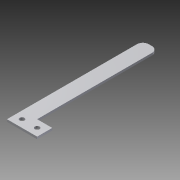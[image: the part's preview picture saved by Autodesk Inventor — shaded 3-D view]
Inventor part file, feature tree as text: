
AUTODESK INVENTOR PART (.ipt)
format: ipt  version: 2015 (Build 190159000, 159)  size: 123,392 bytes
history: native  units: mm
features: sketch x3, extrude x2, other x1, fillet x1, hole x1
ambient origin geometry x8: Origin, YZ Plane, XZ Plane, XY Plane, X Axis, Y Axis, Z Axis, Center Point
bodies: Body1 (feature_tree)
feature tree (8):
  other  "ソリッド1"
  extrude  "押し出し1"  Depth=10.0mm
  fillet  "フィレット1"  Radius=80.0mm
  extrude  "押し出し8"  Depth=1.5mm TaperAngle=0.0deg
  hole  "穴2"  [1 undecoded]
  sketch  "スケッチ1"
  sketch  "スケッチ9"
  sketch  "スケッチ10"
note: 1 required parameter value undecoded (feature->parameter linkage not recoverable at this tier; creation-order binding heuristic only, values carry confidence <= 0.55)
